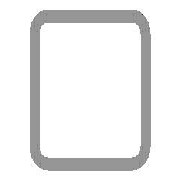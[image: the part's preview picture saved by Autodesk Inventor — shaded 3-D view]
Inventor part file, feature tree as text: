
AUTODESK INVENTOR PART (.ipt)
format: ipt  version: 2025.3 (Build 293356030, 356C)  size: 150,016 bytes
history: native  units: mm (DEFAULTED — no unit token found)
features: other x4, plane x3, split x2, sketch x1
ambient origin geometry x8: Origin, YZ Plane, XZ Plane, XY Plane, X Axis, Y Axis, Z Axis, Center Point
bodies: Solid1 (feature_tree), Body (feature_tree)
feature tree (10):
  parser-record x1  (decoder bookkeeping rows leaked as tree rows — omitted from the tree; the rows remain in map.json)
  other  "Driven Length"
  other  "Start plane"
  other  "End plane"
  plane  "Work Plane4"
  split  "Split1"
  plane  "Work Plane5"
  split  "Split2"
  sketch  "Sketch3"  dims[d3=839.332008mm d4=0.0mm d7=4.0mm d9=40.0mm d11=40.0mm d12=2.0mm d13=193.468323mm d14=1032.800331mm d15=20.0mm d16=20.0mm d17=90.0deg d18=839.332008mm]
  plane  "Work Plane3"
